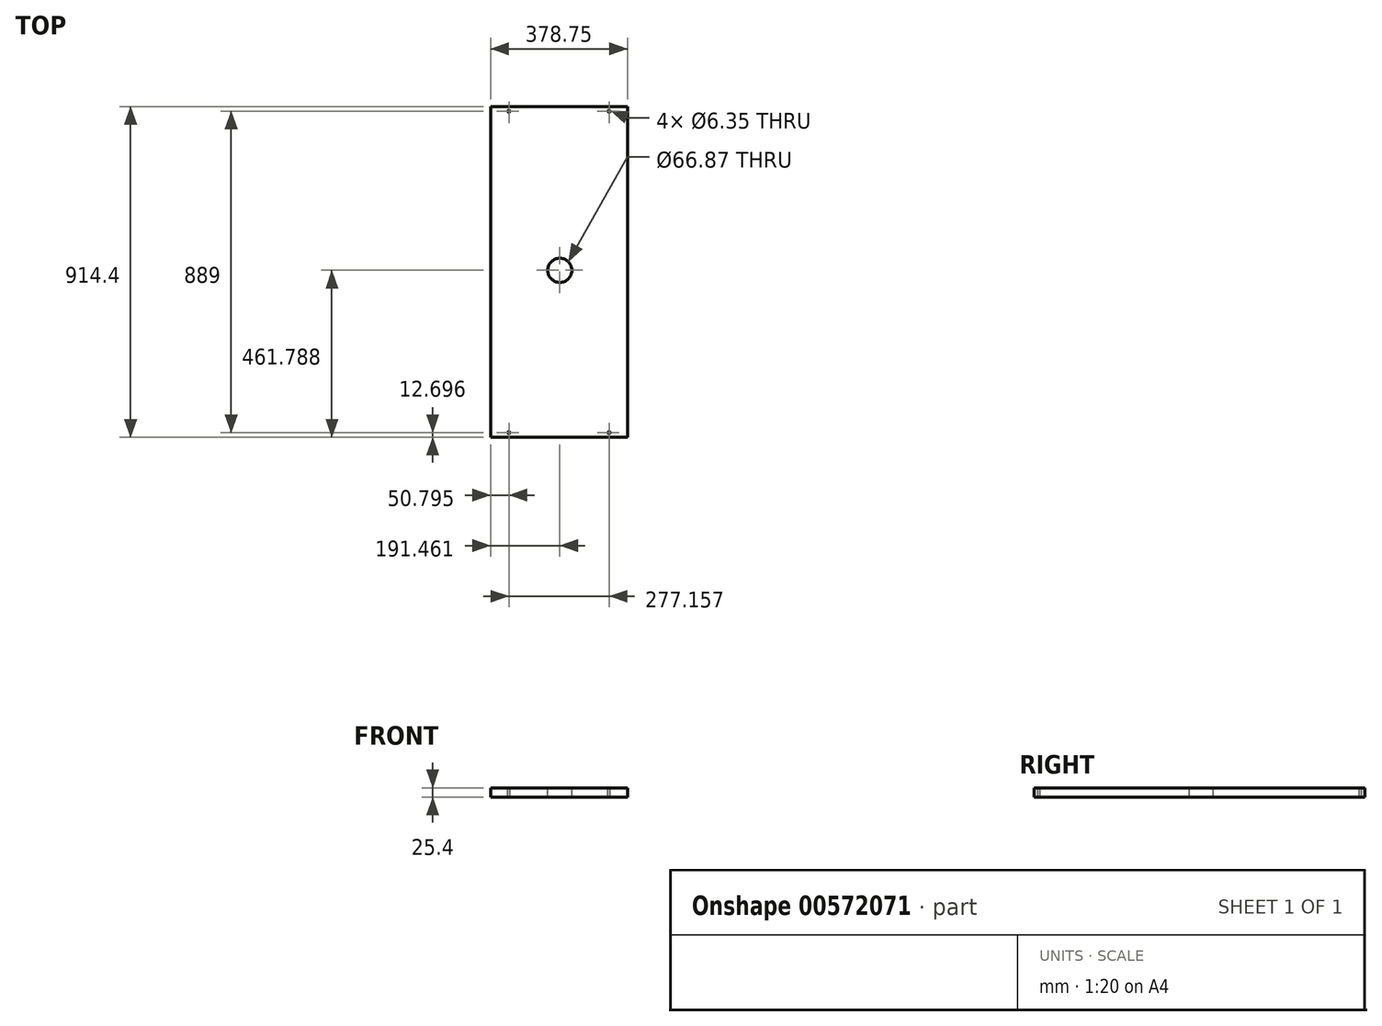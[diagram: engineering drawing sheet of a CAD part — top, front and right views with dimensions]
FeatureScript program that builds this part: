
annotation { "Feature Type Name" : "Feature", "Feature Type Description" : "" }
export const myFeature = defineFeature(function(context is Context, id is Id, definition is map)
    precondition{}
    {
        {
            var Q0;
            Q0=qCreatedBy(makeId("Top.planeOp"),FACE);
            var sketch = newSketch(context, id + "F0", { "sketchPlane" : qUnion([Q0])});
            skLineSegment(sketch, "E0.bottom", {"start": v(185.24, 527.23) * mm, "end": v(-193.51, 527.23) * mm});
            skLineSegment(sketch, "E0.top", {"start": v(185.24, -387.17) * mm, "end": v(-193.51, -387.17) * mm});
            skLineSegment(sketch, "E0.left", {"start": v(185.24, 527.23) * mm, "end": v(185.24, -387.17) * mm});
            skLineSegment(sketch, "E0.right", {"start": v(-193.51, 527.23) * mm, "end": v(-193.51, -387.17) * mm});
            skPoint(sketch, "E0.middle", {"position": v(-4.14, 70.03) * mm});
            skSolve(sketch);
        }
        {
            var Q0;
            Q0=qSketchRegion(id+"F0",true);
            extrude(context, id + "F1", {"entities" : qUnion([Q0]), "depth" : 25.4 * mm, "offsetDistance" : 25.4 * mm});
        }
        {
            var Q0;
            Q0=makeQuery(id+"F1.opExtrude","CAP_FACE",FACE,{"disambiguationData":[OSD([sQuery(id+"F0.wireOp",EDGE,"E0.bottom"),sQuery(id+"F0.wireOp",EDGE,"E0.top"),sQuery(id+"F0.wireOp",EDGE,"E0.left"),sQuery(id+"F0.wireOp",EDGE,"E0.right")])],"isStart":false});
            var sketch = newSketch(context, id + "F2", { "sketchPlane" : qUnion([Q0])});
            skCircle(sketch, "E1", {"center": v(-142.71, 514.53) * mm, "radius": 3.18 * mm});
            skCircle(sketch, "E2", {"center": v(134.44, 514.53) * mm, "radius": 3.17 * mm});
            skCircle(sketch, "E3", {"center": v(-142.71, -374.47) * mm, "radius": 3.17 * mm});
            skCircle(sketch, "E4", {"center": v(134.44, -374.47) * mm, "radius": 3.17 * mm});
            skLineSegment(sketch, "E5", {"start": v(-142.71, 527.23) * mm, "end": v(-142.71, 514.53) * mm});
            skLineSegment(sketch, "E6", {"start": v(-142.71, 511.35) * mm, "end": v(-142.71, 514.53) * mm});
            skLineSegment(sketch, "E7", {"start": v(134.44, 514.53) * mm, "end": v(134.44, 527.23) * mm});
            skLineSegment(sketch, "E8", {"start": v(134.44, 514.53) * mm, "end": v(134.44, 511.35) * mm});
            skLineSegment(sketch, "E9", {"start": v(134.44, -371.3) * mm, "end": v(134.44, -374.47) * mm});
            skLineSegment(sketch, "E10", {"start": v(134.44, -387.17) * mm, "end": v(134.44, -374.47) * mm});
            skLineSegment(sketch, "E11", {"start": v(-142.71, -374.47) * mm, "end": v(-142.71, -377.65) * mm});
            skLineSegment(sketch, "E12", {"start": v(-142.71, -377.65) * mm, "end": v(-142.71, -387.17) * mm});
            skSolve(sketch);
        }
        {
            var Q0;
            Q0 = qSketchRegion(id + "F2", true);
            extrude(context, id + "F3", {"entities" : qUnion([Q0]), "operationType" : NewBodyOperationType.REMOVE, "endBound" : BoundingType.THROUGH_ALL, "oppositeDirection" : true, "depth" : 25.4 * mm, "offsetDistance" : 25.4 * mm});
        }
        {
            var Q0;
            Q0=makeQuery(id+"F1.opExtrude","CAP_FACE",FACE,{"disambiguationData":[OSD([sQuery(id+"F0.wireOp",EDGE,"E0.bottom"),sQuery(id+"F0.wireOp",EDGE,"E0.top"),sQuery(id+"F0.wireOp",EDGE,"E0.left"),sQuery(id+"F0.wireOp",EDGE,"E0.right")])],"isStart":false});
            var sketch = newSketch(context, id + "F4", { "sketchPlane" : qUnion([Q0])});
            skCircle(sketch, "E13", {"center": v(-2.05, 74.62) * mm, "radius": 33.44 * mm});
            skSolve(sketch);
        }
        {
            var Q0;
            Q0 = qSketchRegion(id + "F4", true);
            extrude(context, id + "F5", {"entities" : qUnion([Q0]), "operationType" : NewBodyOperationType.REMOVE, "oppositeDirection" : true, "depth" : 25.4 * mm, "offsetDistance" : 25.4 * mm});
        }
    });
